# Revit family: Sanitary_Taps-Mixers_AXOR_AXOR-MyEdition-Bath-spout___01
name_source: partatom
category: Plumbing Fixtures
revit_build: Autodesk Revit 2018 (Build: 20170223_1515(x64)
units: mm (PartAtom-declared; Revit-internal decimal feet)

## family parameters
Always vertical = No
Cut with Voids When Loaded = No
OmniClass Number = 23.31.11.00
OmniClass Title = Faucets
Part Type = Normal
Room Calculation Point = No
Round Connector Dimension = Use Diameter
Shared = No
Work Plane-Based = Yes

## types (2) — shared parameters
Connector Description = Water Inlet 12.7 mm
Default Elevation = 1219 mm
Description = AXOR MyEdition Bath spout
Diameter = 13 mm
Manufacturer = AXOR
Material = AXOR - Metal - 007 Chrome
Model = 47410CHN
Product Guid = 3c0f454c-0e17-4e51-8cee-557d16d7d514
Product Page URL = https://www.axor-design.com
Product data url = https://bimobject.com
URL = https://www.axor-design.com
Version = 1
zero-valued in all types: Edition number

## per-type parameters (varying)
| type | Material 1 |
| Chrome/Black Glass | AXOR - Glass - Black Glass |
| Chrome/Mirror Glass | AXOR - Glass - Mirror Glass |

## geometry (parser evidence)
native form markers: Sweep x2
no freeform markers — native parametric forms only
